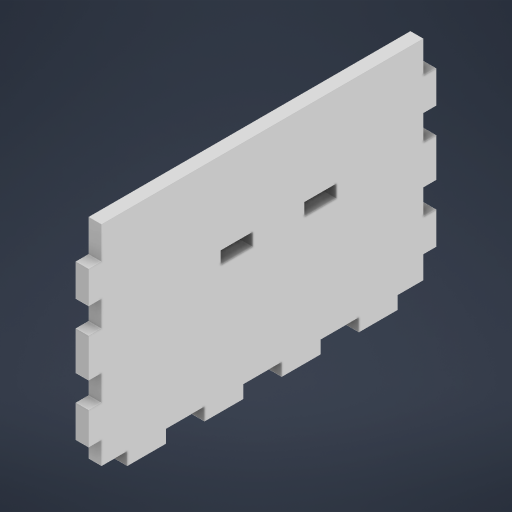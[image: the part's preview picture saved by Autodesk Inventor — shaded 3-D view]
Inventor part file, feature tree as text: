
AUTODESK INVENTOR PART (.ipt)
format: ipt  version: 2023.2 (Build 272271000, 271)  size: 306,176 bytes
history: native  units: mm
features: sketch x2
ambient origin geometry x8: Origin, YZ Plane, XZ Plane, XY Plane, X Axis, Y Axis, Z Axis, Center Point
bodies: Body1 (feature_tree)
feature tree (2):
  sketch  "Sketch1"  dims[d228=69.0mm]
  sketch  "Sketch3"  dims[d229=108.0mm d230=4.0mm d231=0.0mm d246=12.0mm d248=10.0mm d250=8.0mm d253=4.0mm d256=10.0mm d257=12.0mm d259=12.0mm d261=4.0mm d262=0.0mm d264=4.0mm d265=35.5mm d266=26.0mm d267=10.0mm d269=10.0mm d270=4.0mm d271=0.0mm d9=0.5mm d10=0.872665mm d11=0.5mm d12=0.872665mm d13=0.5mm d14=0.872665mm d27=0.5mm d28=0.872665mm d29=0.5mm d30=0.872665mm d88=0.5mm d89=0.872665mm d90=0.5mm d91=0.872665mm d116=0.5mm d117=0.872665mm d118=0.5mm d119=0.872665mm d154=0.5mm d155=0.872665mm d156=0.5mm d157=0.872665mm d181=0.5mm d182=0.872665mm d183=0.5mm d184=0.872665mm d221=0.5mm d222=0.872665mm d223=0.5mm d224=0.872665mm]
